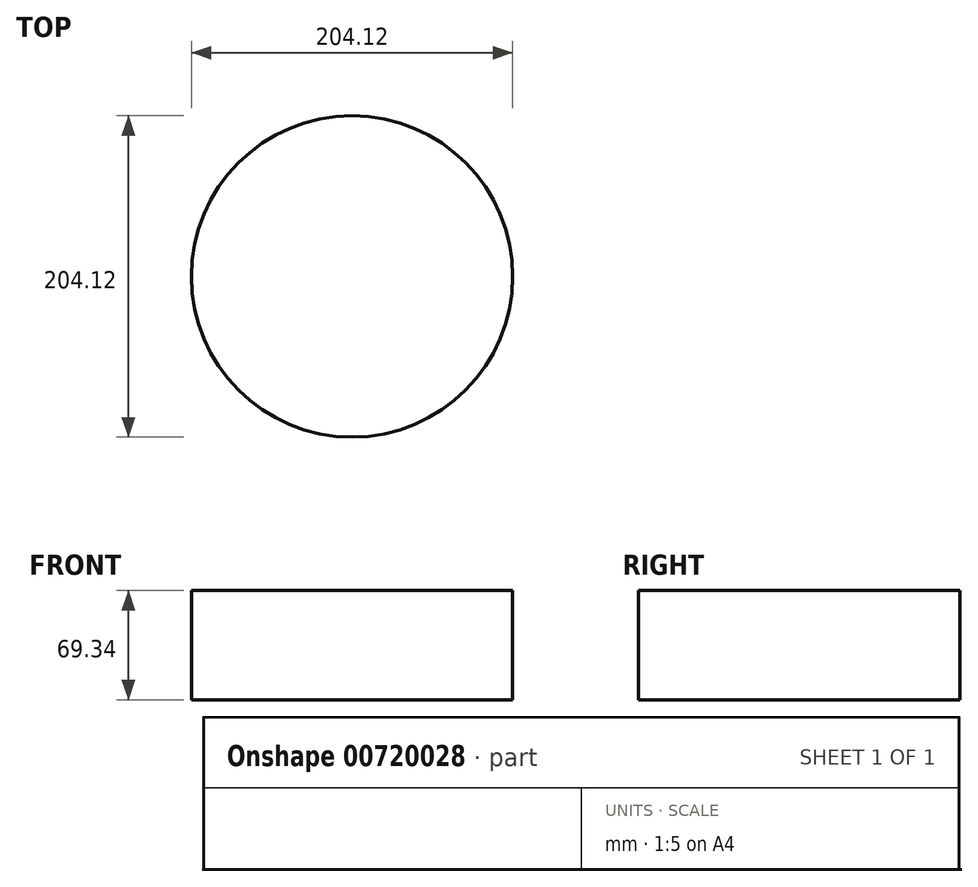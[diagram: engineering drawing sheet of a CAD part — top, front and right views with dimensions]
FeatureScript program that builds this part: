
annotation { "Feature Type Name" : "Feature", "Feature Type Description" : "" }
export const myFeature = defineFeature(function(context is Context, id is Id, definition is map)
    precondition{}
    {
        {
            var Q0;
            Q0=qCreatedBy(makeId("Top.planeOp"),FACE);
            var sketch = newSketch(context, id + "F0", { "sketchPlane" : qUnion([Q0])});
            skCircle(sketch, "E0", {"center": v(0, 0) * mm, "radius": 102.06 * mm});
            skSolve(sketch);
        }
        {
            var Q0;
            Q0=makeQuery(id+"F0.imprint","IMPRINT",FACE,{"disambiguationData":[TD([[makeQuery(id+"F0.imprint","IMPRINT",EDGE,{"derivedFrom":sQuery(id+"F0.wireOp",EDGE,"E0")}),1.0]])]});
            extrude(context, id + "F1", {"entities" : qUnion([Q0]), "depth" : 69.34 * mm, "offsetDistance" : 25.4 * mm});
        }
    });
